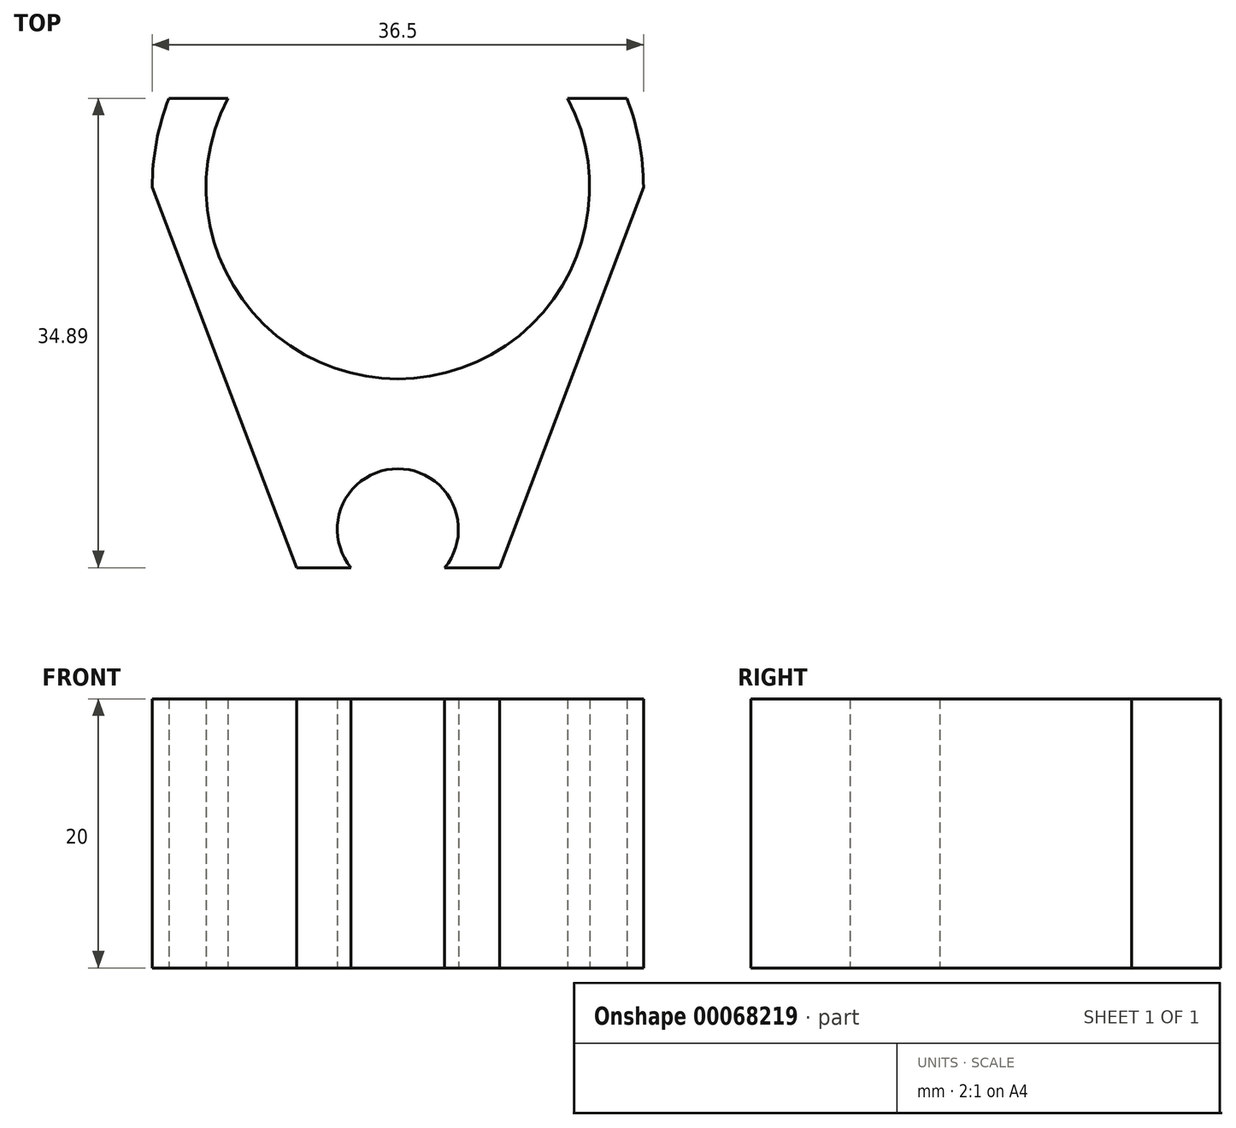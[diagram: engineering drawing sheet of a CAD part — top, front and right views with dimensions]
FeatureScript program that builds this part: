
annotation { "Feature Type Name" : "Feature", "Feature Type Description" : "" }
export const myFeature = defineFeature(function(context is Context, id is Id, definition is map)
    precondition{}
    {
        {
            var Q0;
            Q0=qCreatedBy(makeId("Top.planeOp"),FACE);
            var sketch = newSketch(context, id + "F0", { "sketchPlane" : qUnion([Q0])});
            skArc(sketch, "E0", {"start": v(-12.62, 6.6) * mm, "mid": v(0, -14.25) * mm, "end": v(12.62, 6.6) * mm});
            skArc(sketch, "E1", {"start": v(3.48, -28.28) * mm, "mid": v(0, -20.93) * mm, "end": v(-3.48, -28.28) * mm});
            skLineSegment(sketch, "E2", {"start": v(-18.25, 0) * mm, "end": v(-8.5, -25.7) * mm});
            skLineSegment(sketch, "E3", {"start": v(18.25, 0) * mm, "end": v(8.49, -25.84) * mm});
            skArc(sketch, "E4.trimOffspring", {"start": v(18.25, 0) * mm, "mid": v(17.94, 3.36) * mm, "end": v(17.01, 6.6) * mm});
            skLineSegment(sketch, "E5.bottom", {"start": v(-17.01, 6.6) * mm, "end": v(-12.62, 6.6) * mm});
            skLineSegment(sketch, "E5.top", {"start": v(-7.52, -28.28) * mm, "end": v(-3.48, -28.28) * mm});
            skLineSegment(sketch, "E5.left", {"start": v(-18.22, 1.11) * mm, "end": v(-18.22, -0.09) * mm});
            skLineSegment(sketch, "E5.right", {"start": v(18.21, 1.17) * mm, "end": v(18.21, -0.1) * mm});
            skArc(sketch, "E6.trimOffspring", {"start": v(-17.01, 6.6) * mm, "mid": v(-17.94, 3.36) * mm, "end": v(-18.25, 0) * mm});
            skLineSegment(sketch, "E7.trimOffspring", {"start": v(3.48, -28.28) * mm, "end": v(7.57, -28.28) * mm});
            skLineSegment(sketch, "E8.trimOffspring", {"start": v(12.62, 6.6) * mm, "end": v(17.01, 6.6) * mm});
            skLineSegment(sketch, "E9", {"start": v(-8.5, -25.7) * mm, "end": v(-7.52, -28.28) * mm});
            skLineSegment(sketch, "E10", {"start": v(8.49, -25.84) * mm, "end": v(7.57, -28.28) * mm});
            skSolve(sketch);
        }
        {
            var Q0;
            Q0 = qSketchRegion(id + "F0", true);
            extrude(context, id + "F1", {"entities" : qUnion([Q0]), "depth" : 10 * mm, "hasSecondDirection" : true, "secondDirectionOppositeDirection" : true, "secondDirectionDepth" : 10 * mm});
        }
    });
